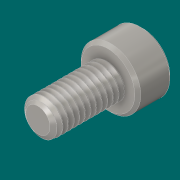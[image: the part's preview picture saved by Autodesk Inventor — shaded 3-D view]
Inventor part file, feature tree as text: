
AUTODESK INVENTOR PART (.ipt)
format: ipt  version: 2016 SP1 (Build 200210100, 210)  size: 472,576 bytes
history: native  units: in
note: dims shown in document units (in); Inventor stores cm internally (conversion verified against a paired STEP export)
features: chamfer x1
ambient origin geometry x8: Origin, YZ Plane, XZ Plane, XY Plane, X Axis, Y Axis, Z Axis, Center Point
bodies: Solid1 (feature_tree)
feature tree (1):
  chamfer  "Chamfer1"  [1 undecoded]
note: 1 required parameter value undecoded (feature->parameter linkage not recoverable at this tier; creation-order binding heuristic only, values carry confidence <= 0.55)
